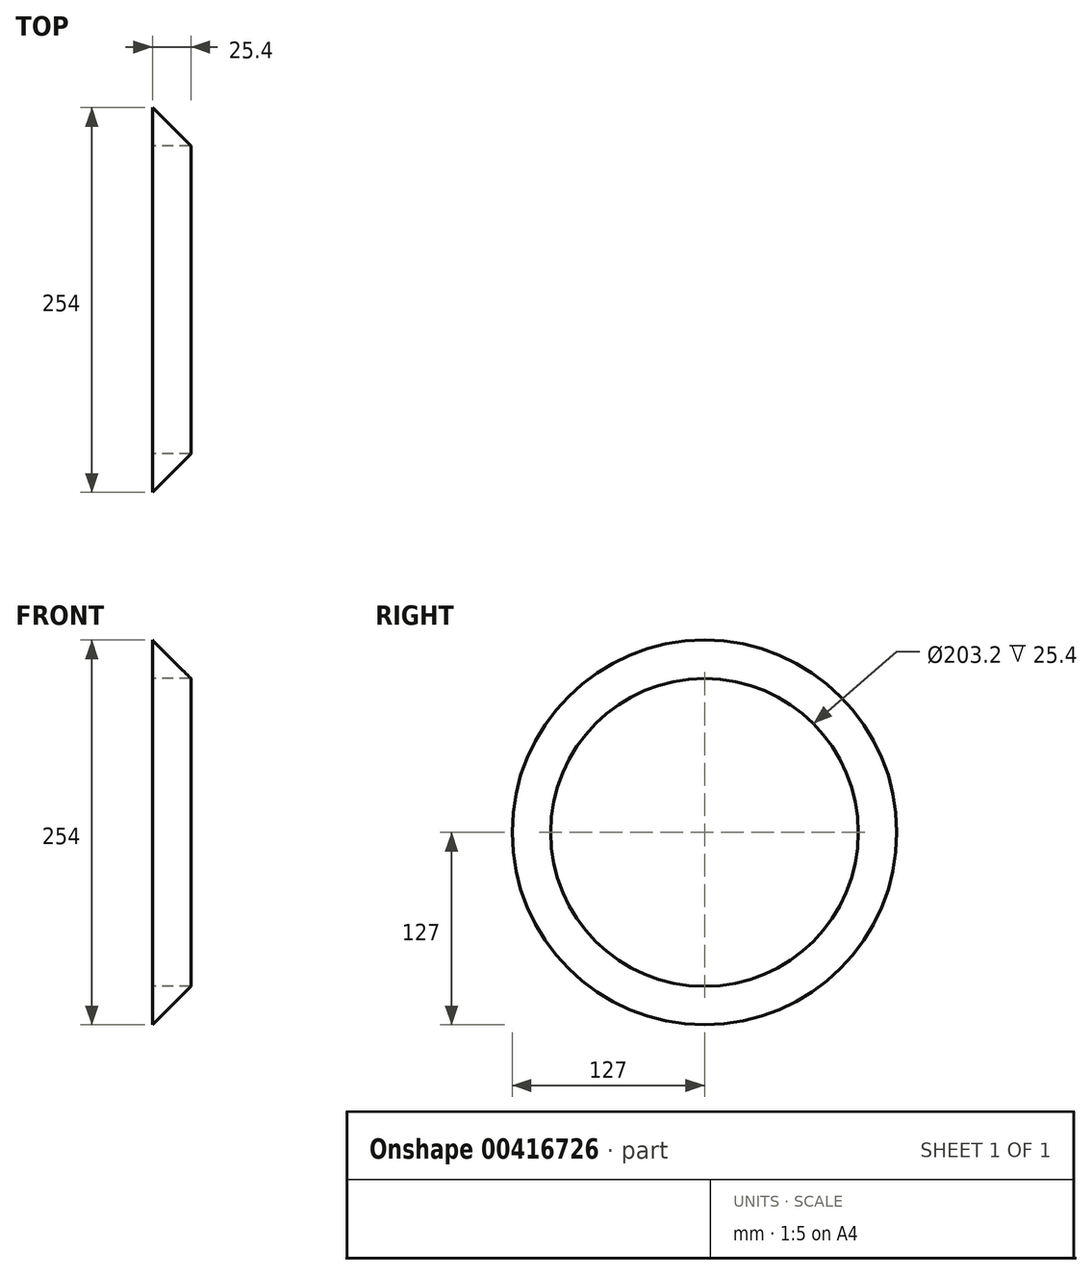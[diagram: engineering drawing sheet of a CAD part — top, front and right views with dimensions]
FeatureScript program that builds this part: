
annotation { "Feature Type Name" : "Feature", "Feature Type Description" : "" }
export const myFeature = defineFeature(function(context is Context, id is Id, definition is map)
    precondition{}
    {
        {
            var Q0;
            Q0=qCreatedBy(makeId("Front.planeOp"),FACE);
            var sketch = newSketch(context, id + "F0", { "sketchPlane" : qUnion([Q0])});
            skLineSegment(sketch, "E0", {"start": v(0, 127) * mm, "end": v(0, 101.6) * mm});
            skLineSegment(sketch, "E1", {"start": v(0, 101.6) * mm, "end": v(25.4, 101.6) * mm});
            skLineSegment(sketch, "E2", {"start": v(25.4, 101.6) * mm, "end": v(0, 127) * mm});
            skSolve(sketch);
        }
        {
            var Q0;
            Q0=qCreatedBy(makeId("Top.planeOp"),FACE);
            var sketch = newSketch(context, id + "F1", { "sketchPlane" : qUnion([Q0])});
            skLineSegment(sketch, "E3", {"start": v(0, 0) * mm, "end": v(63.04, 0) * mm, "construction": true});
            skSolve(sketch);
        }
        {
            var Q0;
            Q0 = qSketchRegion(id + "F0", true);
            var Q1;
            Q1=sQuery(id+"F1.wireOp",EDGE,"E3");
            revolve(context, id + "F2", {"entities" : qUnion([Q0]), "axis" : qUnion([Q1]), "revolveType" : RevolveType.FULL});
        }
    });
